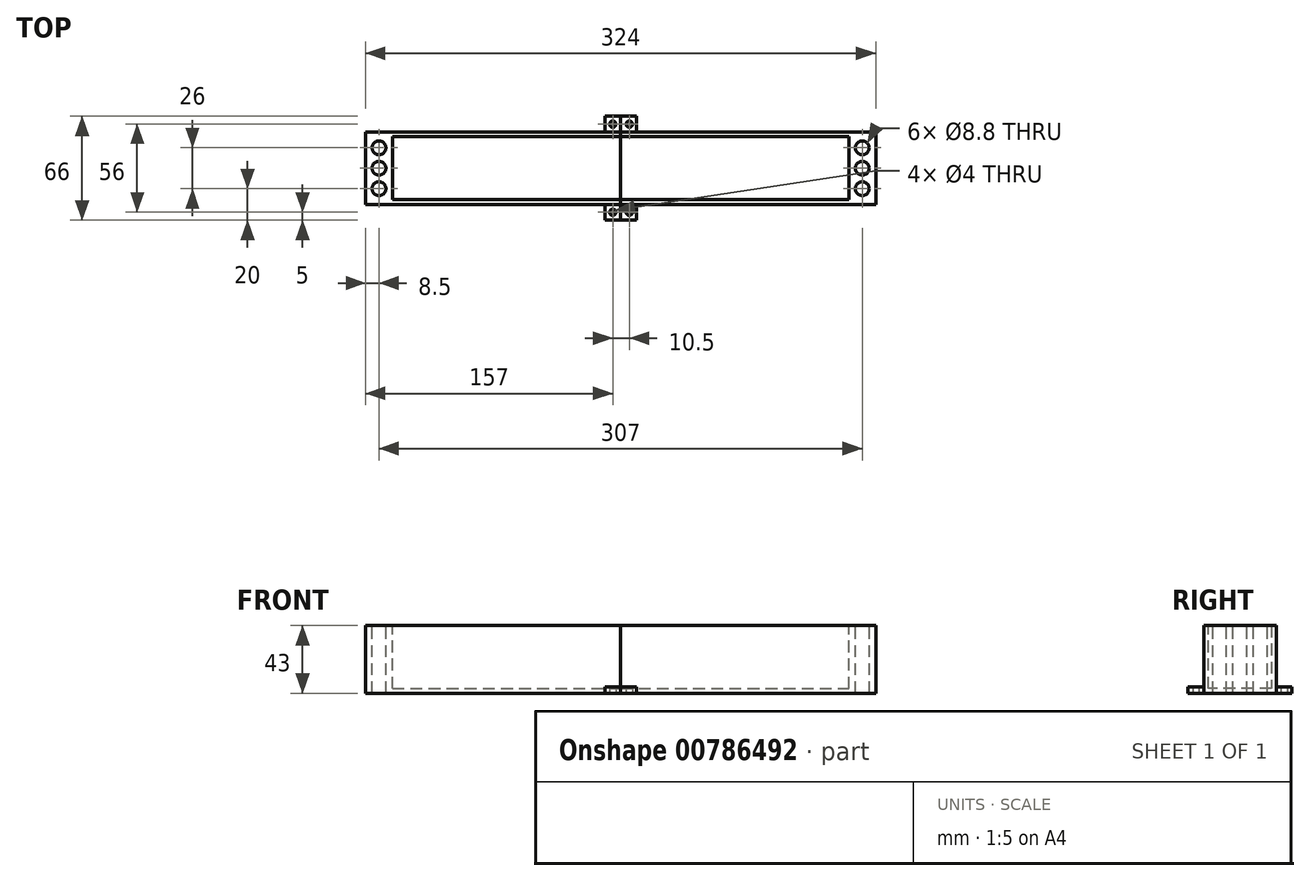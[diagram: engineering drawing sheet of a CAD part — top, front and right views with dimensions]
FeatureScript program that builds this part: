
annotation { "Feature Type Name" : "Feature", "Feature Type Description" : "" }
export const myFeature = defineFeature(function(context is Context, id is Id, definition is map)
    precondition{}
    {
        {
            var Q0;
            Q0=qCreatedBy(makeId("Top.planeOp"),FACE);
            var sketch = newSketch(context, id + "F0", { "sketchPlane" : qUnion([Q0])});
            skLineSegment(sketch, "E0.bottom", {"start": v(-148, 23) * mm, "end": v(148, 23) * mm});
            skLineSegment(sketch, "E0.top", {"start": v(-148, -23) * mm, "end": v(148, -23) * mm});
            skLineSegment(sketch, "E0.left", {"start": v(-148, 23) * mm, "end": v(-148, -23) * mm});
            skLineSegment(sketch, "E0.right", {"start": v(148, 23) * mm, "end": v(148, -23) * mm});
            skSolve(sketch);
        }
        {
            var Q0;
            Q0 = qSketchRegion(id + "F0", true);
            extrude(context, id + "F1", {"entities" : qUnion([Q0]), "depth" : 43 * mm, "offsetDistance" : 25 * mm});
        }
        {
            var Q0;
            Q0=makeQuery(id+"F1.opExtrude","CAP_FACE",FACE,{"disambiguationData":[OSD([sQuery(id+"F0.wireOp",EDGE,"E0.bottom"),sQuery(id+"F0.wireOp",EDGE,"E0.top"),sQuery(id+"F0.wireOp",EDGE,"E0.left"),sQuery(id+"F0.wireOp",EDGE,"E0.right")])],"isStart":false});
            var sketch = newSketch(context, id + "F2", { "sketchPlane" : qUnion([Q0])});
            skLineSegment(sketch, "E1.bottom", {"start": v(-145, 20) * mm, "end": v(145, 20) * mm});
            skLineSegment(sketch, "E1.top", {"start": v(-145, -20) * mm, "end": v(145, -20) * mm});
            skLineSegment(sketch, "E1.left", {"start": v(-145, 20) * mm, "end": v(-145, -20) * mm});
            skLineSegment(sketch, "E1.right", {"start": v(145, 20) * mm, "end": v(145, -20) * mm});
            skSolve(sketch);
        }
        {
            var Q0;
            Q0 = qSketchRegion(id + "F2", true);
            extrude(context, id + "F3", {"entities" : qUnion([Q0]), "operationType" : NewBodyOperationType.REMOVE, "oppositeDirection" : true, "depth" : 40 * mm, "offsetDistance" : 25 * mm});
        }
        {
            var Q0;
            Q0=makeQuery(id+"F1.opExtrude","SWEPT_FACE",FACE,{"disambiguationData":[OSD([sQuery(id+"F0.wireOp",EDGE,"E0.left")])]});
            var sketch = newSketch(context, id + "F4", { "sketchPlane" : qUnion([Q0])});
            skLineSegment(sketch, "E2.bottom", {"start": v(-23, 43) * mm, "end": v(23, 43) * mm});
            skLineSegment(sketch, "E2.top", {"start": v(-23, 0) * mm, "end": v(23, 0) * mm});
            skLineSegment(sketch, "E2.left", {"start": v(-23, 43) * mm, "end": v(-23, 0) * mm});
            skLineSegment(sketch, "E2.right", {"start": v(23, 43) * mm, "end": v(23, 0) * mm});
            skSolve(sketch);
        }
        {
            var Q0;
            Q0 = qSketchRegion(id + "F4", true);
            extrude(context, id + "F5", {"entities" : qUnion([Q0]), "operationType" : NewBodyOperationType.ADD, "depth" : 14 * mm, "offsetDistance" : 25 * mm});
        }
        {
            var Q0;
            Q0=makeQuery(id+"F5.boolean.opBoolean","MERGE",FACE,{"derivedFrom":[makeQuery(id+"F1.opExtrude","CAP_FACE",FACE,{"disambiguationData":[OSD([sQuery(id+"F0.wireOp",EDGE,"E0.bottom"),sQuery(id+"F0.wireOp",EDGE,"E0.top"),sQuery(id+"F0.wireOp",EDGE,"E0.left"),sQuery(id+"F0.wireOp",EDGE,"E0.right")])],"isStart":false}),makeQuery(id+"F5.opExtrude","SWEPT_FACE",FACE,{"disambiguationData":[OSD([sQuery(id+"F4.wireOp",EDGE,"E2.bottom")])]})]});
            var sketch = newSketch(context, id + "F6", { "sketchPlane" : qUnion([Q0])});
            skCircle(sketch, "E3", {"center": v(-153.5, 0) * mm, "radius": 4.4 * mm});
            skPoint(sketch, "E3.centerSnap0", {"position": v(-162, 0) * mm});
            skCircle(sketch, "E4", {"center": v(-153.5, 13) * mm, "radius": 4.4 * mm});
            skCircle(sketch, "E5", {"center": v(-153.5, -13) * mm, "radius": 4.4 * mm});
            skSolve(sketch);
        }
        {
            var Q0;
            Q0 = qSketchRegion(id + "F6", true);
            extrude(context, id + "F7", {"entities" : qUnion([Q0]), "operationType" : NewBodyOperationType.REMOVE, "oppositeDirection" : true, "depth" : 43 * mm, "offsetDistance" : 25 * mm});
        }
        {
            var Q0;
            Q0=makeQuery(id+"F1.opExtrude","SWEPT_BODY",BODY,{"disambiguationData":[OSD([sQuery(id+"F0.wireOp",EDGE,"E0.bottom"),sQuery(id+"F0.wireOp",EDGE,"E0.top"),sQuery(id+"F0.wireOp",EDGE,"E0.left"),sQuery(id+"F0.wireOp",EDGE,"E0.right")])]});
            var Q1;
            Q1=qCreatedBy(makeId("Right.planeOp"),FACE);
            mirror(context, id + "F8", {"operationType" : NewBodyOperationType.ADD, "entities" : qUnion([Q0]), "mirrorPlane" : qUnion([Q1])});
        }
        {
            var Q0;
            {var subQ0=makeQuery(id+"F5.boolean.opBoolean","MERGE",FACE,{"derivedFrom":[makeQuery(id+"F1.opExtrude","SWEPT_FACE",FACE,{"disambiguationData":[OSD([sQuery(id+"F0.wireOp",EDGE,"E0.top")])]}),makeQuery(id+"F5.opExtrude","SWEPT_FACE",FACE,{"disambiguationData":[OSD([sQuery(id+"F4.wireOp",EDGE,"E2.right")])]})]});Q0=makeQuery(id+"F8.boolean.opBoolean","MERGE",FACE,{"derivedFrom":[subQ0,makeQuery(id+"F8.opPattern","COPY",FACE,{"derivedFrom":subQ0,"instanceName":"1"})]});}
            var sketch = newSketch(context, id + "F9", { "sketchPlane" : qUnion([Q0])});
            skLineSegment(sketch, "E6.bottom", {"start": v(-10, 0) * mm, "end": v(10, 0) * mm});
            skLineSegment(sketch, "E6.top", {"start": v(-10, 4) * mm, "end": v(10, 4) * mm});
            skLineSegment(sketch, "E6.left", {"start": v(-10, 0) * mm, "end": v(-10, 4) * mm});
            skLineSegment(sketch, "E6.right", {"start": v(10, 0) * mm, "end": v(10, 4) * mm});
            skSolve(sketch);
        }
        {
            var Q0;
            Q0 = qSketchRegion(id + "F9", true);
            extrude(context, id + "F10", {"entities" : qUnion([Q0]), "operationType" : NewBodyOperationType.ADD, "depth" : 10 * mm, "offsetDistance" : 25 * mm});
        }
        {
            var Q0;
            {var subQ0=makeQuery(id+"F5.boolean.opBoolean","MERGE",FACE,{"derivedFrom":[makeQuery(id+"F1.opExtrude","CAP_FACE",FACE,{"disambiguationData":[OSD([sQuery(id+"F0.wireOp",EDGE,"E0.bottom"),sQuery(id+"F0.wireOp",EDGE,"E0.top"),sQuery(id+"F0.wireOp",EDGE,"E0.left"),sQuery(id+"F0.wireOp",EDGE,"E0.right")])],"isStart":true}),makeQuery(id+"F5.opExtrude","SWEPT_FACE",FACE,{"disambiguationData":[OSD([sQuery(id+"F4.wireOp",EDGE,"E2.top")])]})]});Q0=makeQuery(id+"F10.boolean.opBoolean","MERGE",FACE,{"derivedFrom":[makeQuery(id+"F8.boolean.opBoolean","MERGE",FACE,{"derivedFrom":[subQ0,makeQuery(id+"F8.opPattern","COPY",FACE,{"derivedFrom":subQ0,"instanceName":"1"})]}),makeQuery(id+"F10.opExtrude","SWEPT_FACE",FACE,{"disambiguationData":[OSD([sQuery(id+"F9.wireOp",EDGE,"E6.bottom")])]})]});}
            var sketch = newSketch(context, id + "F11", { "sketchPlane" : qUnion([Q0])});
            skCircle(sketch, "E7", {"center": v(-5, 28) * mm, "radius": 2 * mm});
            skCircle(sketch, "E8", {"center": v(5.5, 28) * mm, "radius": 2 * mm});
            skSolve(sketch);
        }
        {
            var Q0;
            Q0 = qSketchRegion(id + "F11", true);
            extrude(context, id + "F12", {"entities" : qUnion([Q0]), "operationType" : NewBodyOperationType.REMOVE, "oppositeDirection" : true, "depth" : 4 * mm, "offsetDistance" : 25 * mm});
        }
        {
            var Q0;
            Q0=makeQuery(id+"F1.opExtrude","SWEPT_BODY",BODY,{"disambiguationData":[OSD([sQuery(id+"F0.wireOp",EDGE,"E0.bottom"),sQuery(id+"F0.wireOp",EDGE,"E0.top"),sQuery(id+"F0.wireOp",EDGE,"E0.left"),sQuery(id+"F0.wireOp",EDGE,"E0.right")])]});
            var Q1;
            Q1=qCreatedBy(makeId("Front.planeOp"),FACE);
            mirror(context, id + "F13", {"operationType" : NewBodyOperationType.ADD, "entities" : qUnion([Q0]), "mirrorPlane" : qUnion([Q1])});
        }
        {
            var Q0;
            {var subQ0=makeQuery(id+"F5.boolean.opBoolean","MERGE",FACE,{"derivedFrom":[makeQuery(id+"F1.opExtrude","CAP_FACE",FACE,{"disambiguationData":[OSD([sQuery(id+"F0.wireOp",EDGE,"E0.bottom"),sQuery(id+"F0.wireOp",EDGE,"E0.top"),sQuery(id+"F0.wireOp",EDGE,"E0.left"),sQuery(id+"F0.wireOp",EDGE,"E0.right")])],"isStart":true}),makeQuery(id+"F5.opExtrude","SWEPT_FACE",FACE,{"disambiguationData":[OSD([sQuery(id+"F4.wireOp",EDGE,"E2.top")])]})]});var subQ1=makeQuery(id+"F10.boolean.opBoolean","MERGE",FACE,{"derivedFrom":[makeQuery(id+"F8.boolean.opBoolean","MERGE",FACE,{"derivedFrom":[subQ0,makeQuery(id+"F8.opPattern","COPY",FACE,{"derivedFrom":subQ0,"instanceName":"1"})]}),makeQuery(id+"F10.opExtrude","SWEPT_FACE",FACE,{"disambiguationData":[OSD([sQuery(id+"F9.wireOp",EDGE,"E6.bottom")])]})]});Q0=makeQuery(id+"F13.boolean.opBoolean","MERGE",FACE,{"derivedFrom":[subQ1,makeQuery(id+"F13.opPattern","COPY",FACE,{"derivedFrom":subQ1,"instanceName":"1"})]});}
            var sketch = newSketch(context, id + "F14", { "sketchPlane" : qUnion([Q0])});
            skLineSegment(sketch, "E9.bottom", {"start": v(-0.05, 33) * mm, "end": v(0.05, 33) * mm});
            skLineSegment(sketch, "E9.top", {"start": v(-0.05, -33) * mm, "end": v(0.05, -33) * mm});
            skLineSegment(sketch, "E9.left", {"start": v(-0.05, 33) * mm, "end": v(-0.05, -33) * mm});
            skLineSegment(sketch, "E9.right", {"start": v(0.05, 33) * mm, "end": v(0.05, -33) * mm});
            skSolve(sketch);
        }
        {
            var Q0;
            Q0 = qSketchRegion(id + "F14", true);
            extrude(context, id + "F15", {"entities" : qUnion([Q0]), "operationType" : NewBodyOperationType.REMOVE, "oppositeDirection" : true, "depth" : 43 * mm, "offsetDistance" : 25 * mm});
        }
    });
